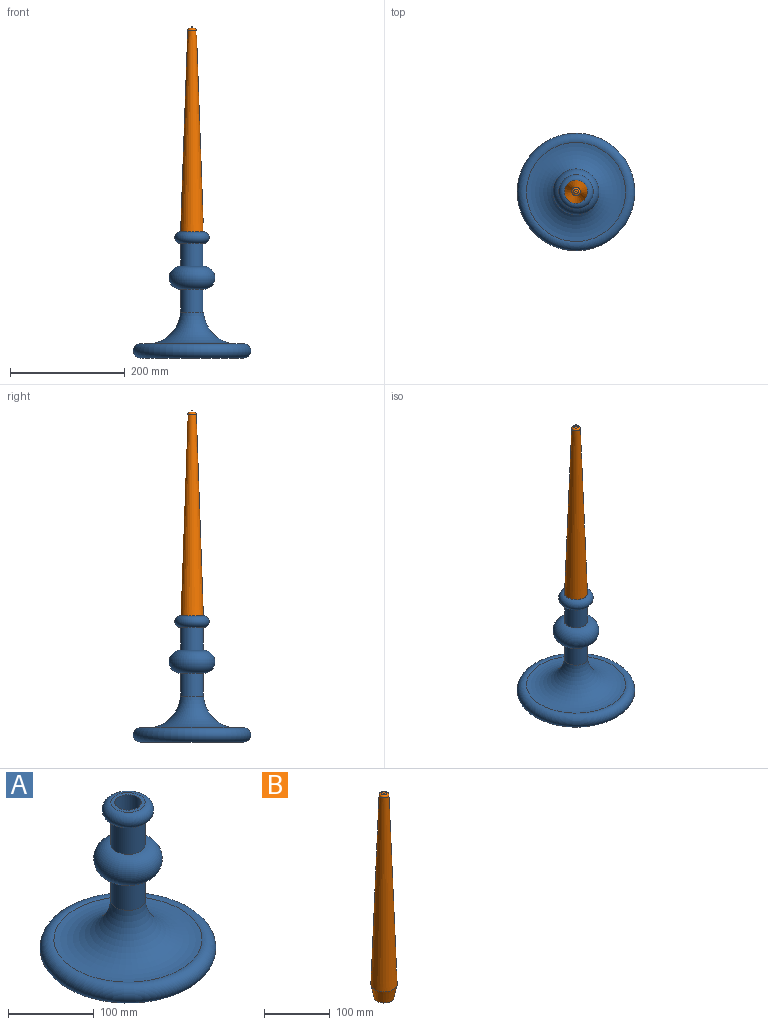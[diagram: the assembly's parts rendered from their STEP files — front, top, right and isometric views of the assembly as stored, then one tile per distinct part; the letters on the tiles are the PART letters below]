
ASSEMBLY  parts=2 mates=1
PART A: 10 faces, bbox 265.1x265.1x220 mm
  f0: plane 180x180mm, normal (0,0,-1), area 25446.9mm2, adj f1
  f1: torus R=90mm, axis (0,0,-1), area 26192.8mm2, adj f0,f2
  f2: torus R=79.86mm, axis (0,0,-1), area 27580.4mm2, adj f1,f3
  f3: cylinder r=20mm len=40mm, axis (0,0,-1), area 5026.5mm2, adj f2,f4
  f4: torus R=20mm, axis (0,0,-1), area 12922.2mm2, adj f3,f5
  f5: cylinder r=20mm len=40mm, axis (0,0,-1), area 5026.5mm2, adj f4,f6
  f6: torus R=20mm, axis (0,0,-1), area 5204.5mm2, adj f5,f7
  f7: plane 40x40mm, normal (0,0,1), area 506.7mm2, adj f6,f8
  f8: cylinder r=15.45mm len=30.9mm, axis (0,0,1), area 2426.9mm2, adj f7,f9
  f9: plane 30.9x30.9mm, normal (0,0,1), area 749.9mm2, adj f8
PART B: 7 faces, bbox 40x40x384.1 mm
  f0: plane 30x30mm, normal (0,0,-1), area 706.9mm2, adj f1
  f1: cone r=15mm half-angle=11.5deg, axis (0,0,1), area 2748.9mm2, adj f0,f2
  f2: cone r=7.5mm half-angle=2deg, axis (0,0,-1), area 30430.2mm2, adj f1,f3
  f3: torus R=4mm, axis (0,0,-1), area 215.1mm2, adj f2,f4
  f4: plane 8x8mm, normal (0,0,1), area 49.9mm2, adj f3,f5
  f5: cylinder r=0.34mm len=3.7mm, axis (0,0,-1), area 7.8mm2, adj f4,f6
  f6: cone r=0mm half-angle=37.6deg, axis (0,0,-1), area 0.6mm2, adj f5
PLACE A t=(-26.43,36.77,-31.95)mm
PLACE B t=(-26.43,36.77,163.05)mm
MATE fastened B.f1 <-> A.f8  axis (0,0,-1) through (-26.43,36.77,163.05)mm
